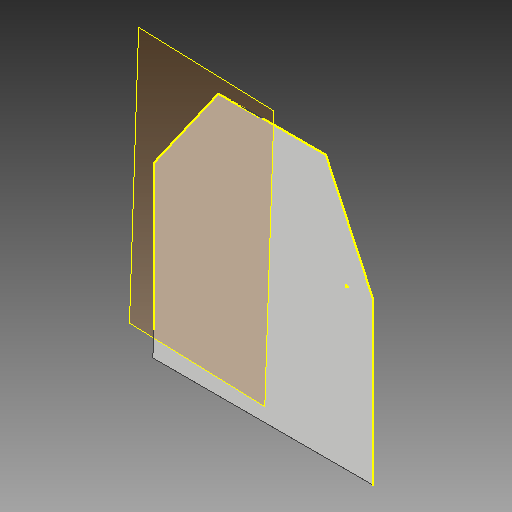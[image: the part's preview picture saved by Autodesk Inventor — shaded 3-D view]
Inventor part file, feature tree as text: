
AUTODESK INVENTOR PART (.ipt)
format: ipt  version: 2018 (Build 220112000, 112)  size: 118,272 bytes
history: native  units: mm
features: reference x11, other x6, sketch x2, plane x1, extrude x1
ambient origin geometry x8: Origin, YZ Plane, XZ Plane, XY Plane, X Axis, Y Axis, Z Axis, Center Point
bodies: Solid1 (feature_tree)
feature tree (21):
  other  "Table"
  other  "cover end plates-01"
  other  "cover end plates-02"
  plane  "Work Plane1"
  sketch  "Sketch1"  dims[d0=1.6mm d1=0.0mm]
  extrude  "Extrusion1"  [1 undecoded]
  reference  "Reference1"
  reference  "Reference2"
  reference  "Reference3"
  reference  "Reference4"
  reference  "Reference5"
  reference  "Reference6"
  sketch  "Sketch2"
  reference  "Reference7"
  reference  "Reference8"
  reference  "Reference9"
  reference  "Reference10"
  reference  "Reference11"
  other  "Lathe Model 2018.iam"
  other  "polycarbonate cover:1"
  other  "back plate:1"
note: 1 required parameter value undecoded (feature->parameter linkage not recoverable at this tier; creation-order binding heuristic only, values carry confidence <= 0.55)
